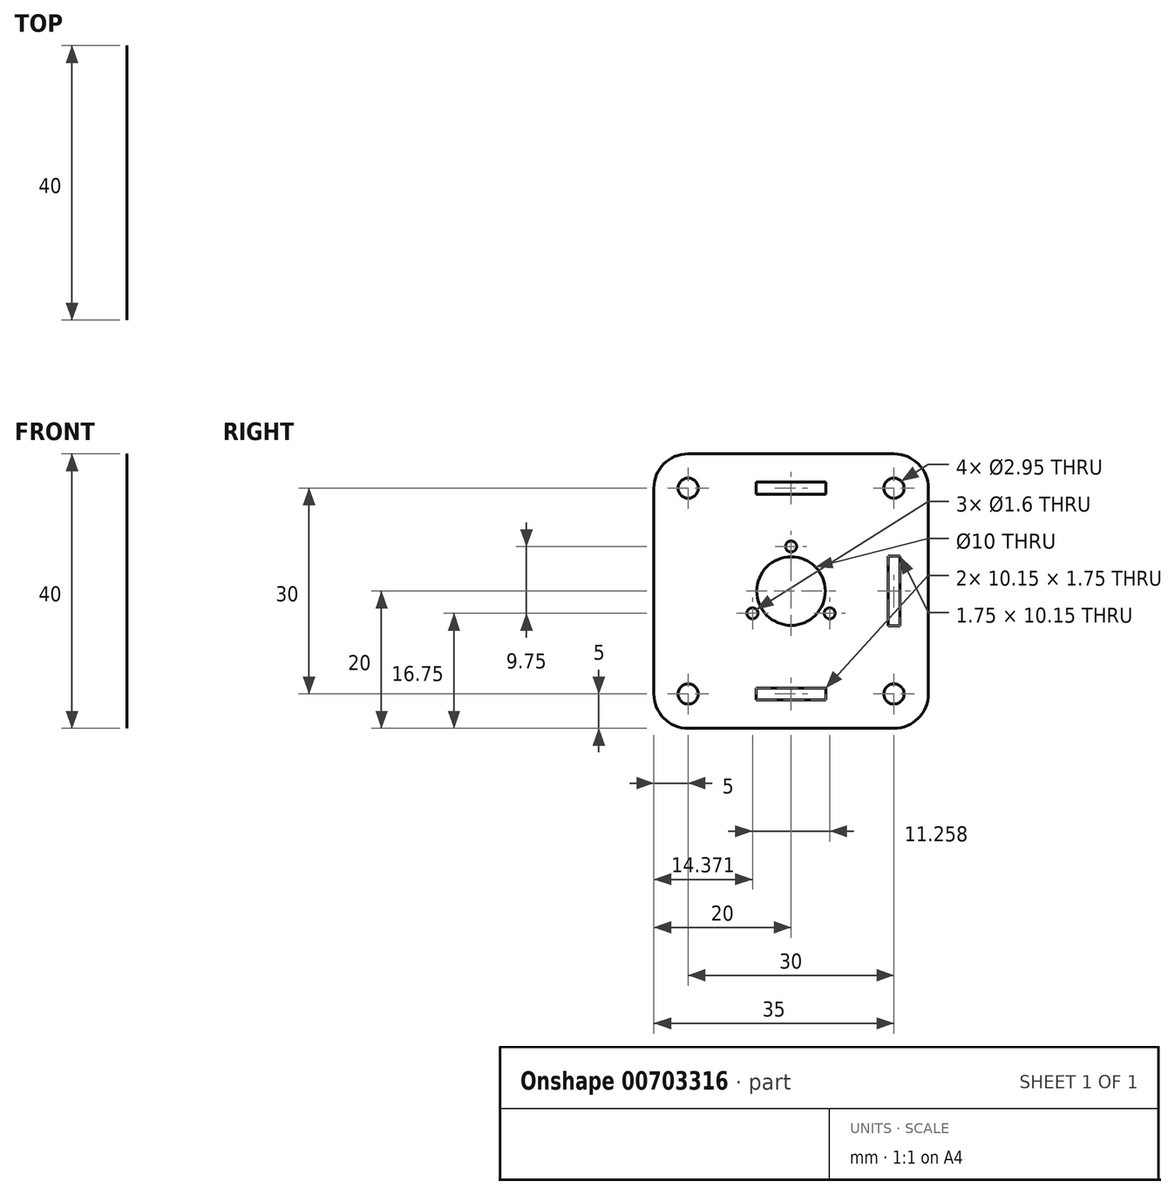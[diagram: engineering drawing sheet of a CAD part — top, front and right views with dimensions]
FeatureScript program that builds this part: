
annotation { "Feature Type Name" : "Feature", "Feature Type Description" : "" }
export const myFeature = defineFeature(function(context is Context, id is Id, definition is map)
    precondition{}
    {
        {
            var Q0;
            Q0=qCreatedBy(makeId("Right.planeOp"),FACE);
            var sketch = newSketch(context, id + "F0", { "sketchPlane" : qUnion([Q0])});
            skPoint(sketch, "E0.middle", {"position": v(0, 0) * mm});
            skCircle(sketch, "E1", {"center": v(0, 0) * mm, "radius": 5 * mm});
            skCircle(sketch, "E2", {"center": v(-15, 15) * mm, "radius": 1.47 * mm});
            skCircle(sketch, "E3", {"center": v(15, 15) * mm, "radius": 1.47 * mm});
            skCircle(sketch, "E4", {"center": v(15, -15) * mm, "radius": 1.47 * mm});
            skCircle(sketch, "E5", {"center": v(-15, -15) * mm, "radius": 1.47 * mm});
            skCircle(sketch, "E6", {"center": v(0, 6.5) * mm, "radius": 0.8 * mm});
            skLineSegment(sketch, "E7", {"start": v(0, 0) * mm, "end": v(0, 0) * mm});
            skCircle(sketch, "E8", {"center": v(-5.63, -3.25) * mm, "radius": 0.8 * mm});
            skCircle(sketch, "E9", {"center": v(5.63, -3.25) * mm, "radius": 0.8 * mm});
            skLineSegment(sketch, "E10.bottom", {"start": v(-20, -20) * mm, "end": v(20, -20) * mm});
            skLineSegment(sketch, "E10.top", {"start": v(-20, 20) * mm, "end": v(20, 20) * mm});
            skLineSegment(sketch, "E10.left", {"start": v(-20, -20) * mm, "end": v(-20, 20) * mm});
            skLineSegment(sketch, "E10.right", {"start": v(20, -20) * mm, "end": v(20, 20) * mm});
            skLineSegment(sketch, "E11.bottom", {"start": v(5.08, 14.13) * mm, "end": v(-5.08, 14.13) * mm});
            skLineSegment(sketch, "E11.top", {"start": v(5.08, 15.87) * mm, "end": v(-5.08, 15.87) * mm});
            skLineSegment(sketch, "E11.left", {"start": v(5.08, 14.13) * mm, "end": v(5.08, 15.87) * mm});
            skLineSegment(sketch, "E11.right", {"start": v(-5.08, 14.13) * mm, "end": v(-5.08, 15.87) * mm});
            skPoint(sketch, "E11.middle", {"position": v(0, 15) * mm});
            skLineSegment(sketch, "E12.bottom", {"start": v(15.87, 5.07) * mm, "end": v(14.13, 5.07) * mm});
            skLineSegment(sketch, "E12.top", {"start": v(15.87, -5.08) * mm, "end": v(14.13, -5.08) * mm});
            skLineSegment(sketch, "E12.left", {"start": v(15.87, 5.07) * mm, "end": v(15.87, -5.08) * mm});
            skLineSegment(sketch, "E12.right", {"start": v(14.13, 5.07) * mm, "end": v(14.13, -5.08) * mm});
            skPoint(sketch, "E12.middle", {"position": v(15, 0) * mm});
            skLineSegment(sketch, "E13.bottom", {"start": v(5.08, -15.87) * mm, "end": v(-5.08, -15.87) * mm});
            skLineSegment(sketch, "E13.top", {"start": v(5.08, -14.13) * mm, "end": v(-5.08, -14.13) * mm});
            skLineSegment(sketch, "E13.left", {"start": v(5.08, -15.87) * mm, "end": v(5.08, -14.13) * mm});
            skLineSegment(sketch, "E13.right", {"start": v(-5.08, -15.87) * mm, "end": v(-5.08, -14.13) * mm});
            skPoint(sketch, "E13.middle", {"position": v(0, -15) * mm});
            skLineSegment(sketch, "E14", {"start": v(0, 0) * mm, "end": v(0, 6.5) * mm});
            skLineSegment(sketch, "E15", {"start": v(5.63, -3.25) * mm, "end": v(0, 0) * mm});
            skLineSegment(sketch, "E16", {"start": v(0, 0) * mm, "end": v(-5.63, -3.25) * mm});
            skSolve(sketch);
        }
        {
            var Q0;
            Q0=makeQuery(id+"F0.imprint","IMPRINT",FACE,{"disambiguationData":[TD([[makeQuery(id+"F0.imprint","IMPRINT",EDGE,{"derivedFrom":sQuery(id+"F0.wireOp",EDGE,"E2")}),-1.0]])]});
            extrude(context, id + "F1", {"entities" : qUnion([Q0]), "endBound" : BoundingType.SYMMETRIC, "depth" : 1 / 406.4 * mm, "offsetDistance" : 25 * mm});
        }
        {
            var Q0;
            Q0=makeQuery(id+"F1.opExtrude","SWEPT_EDGE",EDGE,{"disambiguationData":[OSD([sQuery(id+"F0.wireOp",EDGE,"E10.top"),sQuery(id+"F0.wireOp",EDGE,"E10.left")])]});
            var Q1;
            Q1=makeQuery(id+"F1.opExtrude","SWEPT_EDGE",EDGE,{"disambiguationData":[OSD([sQuery(id+"F0.wireOp",EDGE,"E10.top"),sQuery(id+"F0.wireOp",EDGE,"E10.right")])]});
            var Q2;
            Q2=makeQuery(id+"F1.opExtrude","SWEPT_EDGE",EDGE,{"disambiguationData":[OSD([sQuery(id+"F0.wireOp",EDGE,"E10.bottom"),sQuery(id+"F0.wireOp",EDGE,"E10.left")])]});
            var Q3;
            Q3=makeQuery(id+"F1.opExtrude","SWEPT_EDGE",EDGE,{"disambiguationData":[OSD([sQuery(id+"F0.wireOp",EDGE,"E10.bottom"),sQuery(id+"F0.wireOp",EDGE,"E10.right")])]});
            fillet(context, id + "F2", {"entities" : qUnion([Q0, Q1, Q2, Q3]), "radius" : 5 * mm, "tangentPropagation" : true, "allowEdgeOverflow" : false});
        }
    });
